AUTODESK INVENTOR PART (.ipt)
format: ipt  version: 2023 (Build 270158000, 158)  size: 234,496 bytes
history: native  units: mm
features: other x4, plane x3, sketch x3, split x2
ambient origin geometry x8: Origin, YZ Plane, XZ Plane, XY Plane, X Axis, Y Axis, Z Axis, Center Point
bodies: Solid1 (feature_tree), Body (feature_tree)
feature tree (12):
  other  "Driven Length"
  other  "Frame Generator"
  other  "Start Plane"
  other  "End Plane"
  plane  "Work Plane5"
  split  "Split1"
  plane  "Work Plane6"
  split  "Split2"
  sketch  "Sketch"  dims[d5=7.0mm d6=2.0mm d7=0.5mm d8=1.0mm d9=20.0mm d10=20.0mm d11=8.0mm d13=5.0mm d14=8.0mm d17=10.0mm d18=289.4mm d19=0.13mm d20=0.0mm d23=90.0deg d22=279.4mm]
  sketch  "Sketch4"  dims[d3=2.0mm]
  plane  "Work Plane4"
  sketch  "Sketch5"  dims[d4=2.0mm]
